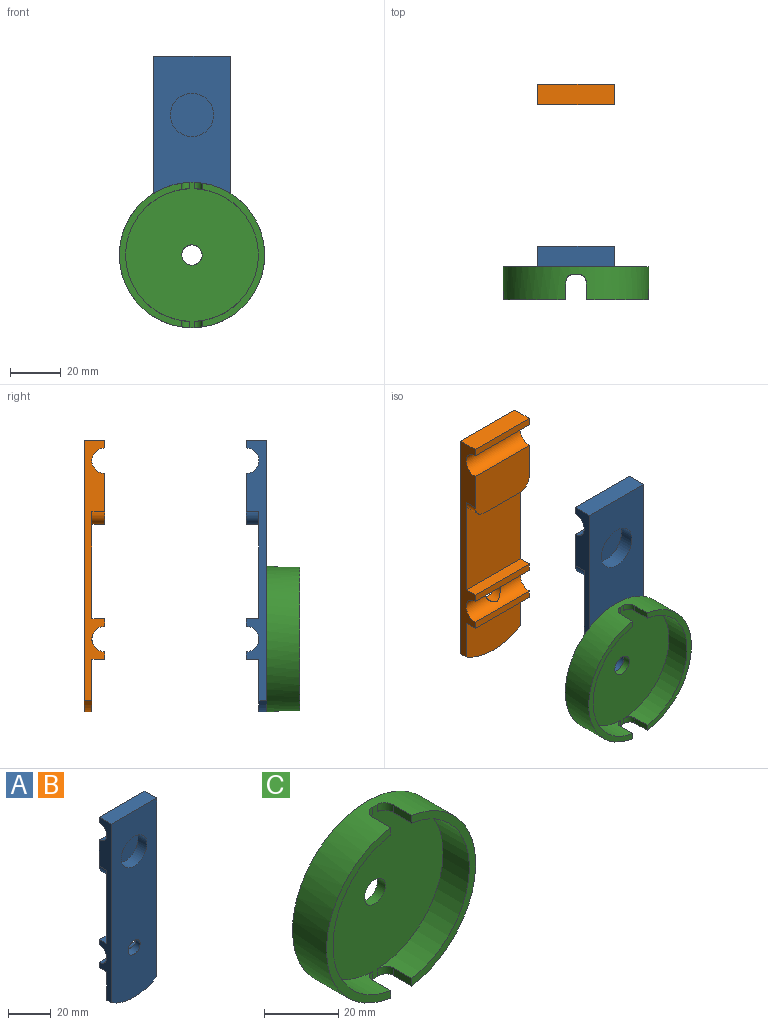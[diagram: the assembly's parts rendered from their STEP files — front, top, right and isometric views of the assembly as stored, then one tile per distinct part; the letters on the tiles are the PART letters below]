
ASSEMBLY  parts=3 mates=2
PART A: 21 faces, bbox 30x8x106.5 mm
  f0: plane 102.23x8mm, normal (1,0,0), area 448.2mm2, adj f1,f3,f4,f5,f6,f7,f8,f9
  f1: plane 30x20.5mm, normal (0,1,0), area 573.7mm2, adj f0,f2,f8,f20
  f2: plane 102.23x8mm, normal (-1,0,0), area 448.2mm2, adj f1,f3,f4,f5,f6,f7,f8,f9
  f3: plane 30x3mm, normal (0,1,0), area 90mm2, adj f0,f2,f8,f17
  f4: plane 30x3mm, normal (0,1,0), area 90mm2, adj f0,f2,f9,f17
  f5: plane 30x20mm, normal (0,1,0), area 589.3mm2, adj f0,f2,f11,f16,f18,f19
  f6: plane 30x3mm, normal (0,1,0), area 90mm2, adj f0,f2,f12,f16
  f7: plane 106.5x30mm, normal (0,-1,0), area 2876.5mm2, adj f0,f2,f12,f13,f15,f20
  f8: plane 30x5mm, normal (0,0,-1), area 150mm2, adj f0,f1,f2,f3
  f9: plane 30x5mm, normal (0,0,1), area 150mm2, adj f0,f2,f4,f10
  f10: plane 42x30mm, normal (0,1,0), area 1120.7mm2, adj f0,f2,f9,f11,f18,f19
  f11: plane 20x5mm, normal (0,0,-1), area 100mm2, adj f5,f10,f18,f19
  f12: plane 30x8mm, normal (0,0,1), area 240mm2, adj f0,f2,f6,f7
  f13: cylinder r=8.5mm len=17mm, axis (0,-1,0), area 315.1mm2, adj f7,f14
  f14: plane 17x17mm, normal (0,-1,0), area 227mm2, adj f13
  f15: cylinder r=4mm len=8mm, axis (0,-1,0), area 99mm2, adj f7,f17
  f16: cylinder r=5mm len=30mm, axis (-1,0,0), area 471.2mm2, adj f0,f2,f5,f6
  f17: cylinder r=5mm len=30mm, axis (-1,0,0), area 415.4mm2, adj f0,f2,f3,f4,f15
  f18: cylinder r=5mm len=5mm, axis (0,1,0), area 39.3mm2, adj f2,f5,f10,f11
  f19: cylinder r=5mm len=5mm, axis (0,-1,0), area 39.3mm2, adj f0,f5,f10,f11
  f20: cylinder r=28.5mm len=30mm, axis (0,1,0), area 94.8mm2, adj f0,f1,f2,f7
PART B: same geometry as A
PART C: 16 faces, bbox 57x13x57 mm
  f0: plane 56.44x24.5mm, normal (0,-1,0), area 190.3mm2, adj f1,f2,f10,f12
  f1: cylinder r=26.05mm len=52.06mm, axis (0,-1,0), area 742mm2, adj f0,f6,f9,f10,f12,f14
  f2: cylinder r=28.5mm len=57mm, axis (0,1,0), area 2175.2mm2, adj f0,f3,f4,f6,f7,f8,f9,f10
  f3: plane 56.44x24.5mm, normal (0,-1,0), area 190.3mm2, adj f2,f5,f8,f11
  f4: plane 57x57mm, normal (0,1,0), area 2501.5mm2, adj f2,f15
  f5: cylinder r=26.05mm len=52.06mm, axis (0,-1,0), area 742mm2, adj f3,f6,f7,f8,f11,f13
  f6: plane 57x52.1mm, normal (0,-1,0), area 2091.4mm2, adj f1,f2,f5,f7,f9,f13,f14,f15
  f7: cylinder r=3mm len=3mm, axis (0,0,-1), area 11.6mm2, adj f2,f5,f6,f8
  f8: plane 7x2.48mm, normal (1,0,0), area 17.3mm2, adj f2,f3,f5,f7
  f9: cylinder r=3mm len=3mm, axis (0,0,1), area 11.6mm2, adj f1,f2,f6,f10
  f10: plane 7x2.48mm, normal (-1,0,0), area 17.3mm2, adj f0,f1,f2,f9
  f11: plane 7x2.48mm, normal (1,0,0), area 17.3mm2, adj f2,f3,f5,f13
  f12: plane 7x2.48mm, normal (-1,0,0), area 17.3mm2, adj f0,f1,f2,f14
  f13: cylinder r=3mm len=3mm, axis (0,0,-1), area 11.6mm2, adj f2,f5,f6,f11
  f14: cylinder r=3mm len=3mm, axis (0,0,1), area 11.6mm2, adj f1,f2,f6,f12
  f15: cylinder r=4mm len=8mm, axis (0,-1,0), area 75.4mm2, adj f4,f6
PLACE A t=(0,-99,0)mm
PLACE B rot(axis=(0,0,1),180deg) t=(0,-27.4,0)mm
PLACE C t=(0,-99,0)mm fixed
MATE slider A.f5 <-> B.f5  axis (0,1,0) through (0,-91,55.16)mm
MATE fastened A.f15 <-> C.f1  axis (0,-1,0) through (0,-99,0)mm
